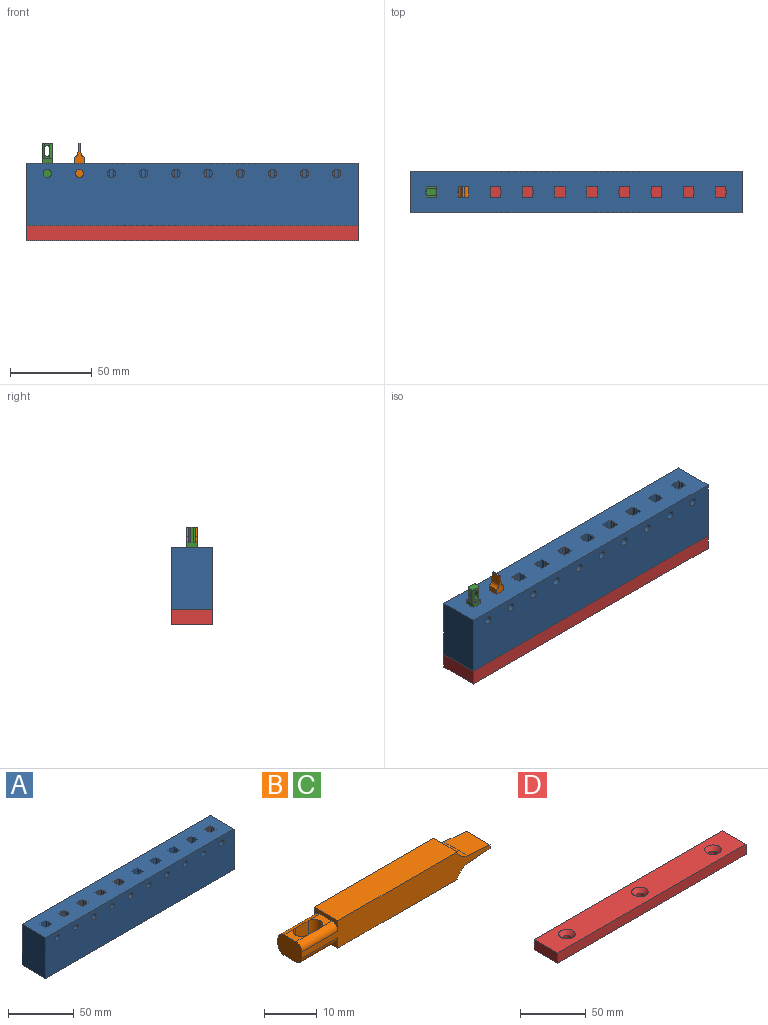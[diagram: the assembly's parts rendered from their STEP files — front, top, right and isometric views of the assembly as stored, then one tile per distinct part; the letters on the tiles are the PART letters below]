
ASSEMBLY  parts=4 mates=9
PART A: 152 faces, bbox 203.2x25.4x38.1 mm
  f0: plane 38.1x2.04mm, normal (0,-1,0), area 77.6mm2, adj f40,f41,f49,f151
  f1: plane 38.1x2.04mm, normal (1,0,0), area 77.6mm2, adj f40,f41,f48,f150
  f2: plane 38.1x2.04mm, normal (0,1,0), area 73mm2, adj f3,f40,f41,f95,f102,f103
  f3: plane 38.1x2.04mm, normal (-1,0,0), area 77.6mm2, adj f2,f40,f41,f149
  f4: plane 38.1x2.04mm, normal (0,-1,0), area 77.6mm2, adj f40,f41,f53,f148
  f5: plane 38.1x2.04mm, normal (1,0,0), area 77.6mm2, adj f40,f41,f52,f147
  f6: plane 38.1x2.04mm, normal (0,1,0), area 73mm2, adj f7,f40,f41,f94,f104,f105
  f7: plane 38.1x2.04mm, normal (-1,0,0), area 77.6mm2, adj f6,f40,f41,f146
  f8: plane 38.1x2.04mm, normal (0,-1,0), area 77.6mm2, adj f40,f41,f57,f145
  f9: plane 38.1x2.04mm, normal (1,0,0), area 77.6mm2, adj f40,f41,f56,f144
  f10: plane 38.1x2.04mm, normal (0,1,0), area 73mm2, adj f11,f40,f41,f93,f106,f107
  f11: plane 38.1x2.04mm, normal (-1,0,0), area 77.6mm2, adj f10,f40,f41,f143
  f12: plane 38.1x2.04mm, normal (0,-1,0), area 77.6mm2, adj f40,f41,f61,f142
  f13: plane 38.1x2.04mm, normal (1,0,0), area 77.6mm2, adj f40,f41,f60,f141
  f14: plane 38.1x2.04mm, normal (0,1,0), area 73mm2, adj f15,f40,f41,f92,f108,f109
  f15: plane 38.1x2.04mm, normal (-1,0,0), area 77.6mm2, adj f14,f40,f41,f140
  f16: plane 38.1x2.04mm, normal (0,-1,0), area 77.6mm2, adj f40,f41,f65,f139
  f17: plane 38.1x2.04mm, normal (1,0,0), area 77.6mm2, adj f40,f41,f64,f138
  f18: plane 38.1x2.04mm, normal (0,1,0), area 73mm2, adj f19,f40,f41,f91,f110,f111
  f19: plane 38.1x2.04mm, normal (-1,0,0), area 77.6mm2, adj f18,f40,f41,f137
  f20: plane 38.1x2.04mm, normal (0,-1,0), area 77.6mm2, adj f40,f41,f69,f136
  f21: plane 38.1x2.04mm, normal (1,0,0), area 77.6mm2, adj f40,f41,f68,f135
  f22: plane 38.1x2.04mm, normal (0,1,0), area 73mm2, adj f23,f40,f41,f90,f112,f113
  f23: plane 38.1x2.04mm, normal (-1,0,0), area 77.6mm2, adj f22,f40,f41,f134
  f24: plane 38.1x2.04mm, normal (0,-1,0), area 77.6mm2, adj f40,f41,f73,f133
  f25: plane 38.1x2.04mm, normal (1,0,0), area 77.6mm2, adj f40,f41,f72,f132
  f26: plane 38.1x2.04mm, normal (0,1,0), area 73mm2, adj f27,f40,f41,f89,f114,f115
  f27: plane 38.1x2.04mm, normal (-1,0,0), area 77.6mm2, adj f26,f40,f41,f131
  f28: plane 38.1x2.04mm, normal (0,-1,0), area 77.6mm2, adj f40,f41,f77,f130
  f29: plane 38.1x2.04mm, normal (1,0,0), area 77.6mm2, adj f40,f41,f76,f129
  f30: plane 38.1x2.04mm, normal (0,1,0), area 73mm2, adj f31,f40,f41,f88,f116,f117
  f31: plane 38.1x2.04mm, normal (-1,0,0), area 77.6mm2, adj f30,f40,f41,f128
  f32: plane 38.1x2.04mm, normal (0,-1,0), area 77.6mm2, adj f40,f41,f81,f127
  f33: plane 38.1x2.04mm, normal (1,0,0), area 77.6mm2, adj f40,f41,f80,f126
  f34: plane 38.1x2.04mm, normal (0,1,0), area 73mm2, adj f35,f40,f41,f87,f118,f119
  f35: plane 38.1x2.04mm, normal (-1,0,0), area 77.6mm2, adj f34,f40,f41,f125
  f36: plane 38.1x2.04mm, normal (0,-1,0), area 77.6mm2, adj f40,f41,f85,f124
  f37: plane 38.1x2.04mm, normal (1,0,0), area 77.6mm2, adj f40,f41,f84,f123
  f38: plane 38.1x2.04mm, normal (0,1,0), area 73mm2, adj f39,f40,f41,f86,f120,f121
  f39: plane 38.1x2.04mm, normal (-1,0,0), area 77.6mm2, adj f38,f40,f41,f122
  f40: plane 203.2x25.4mm, normal (0,0,1), area 4745.9mm2, adj f0,f1,f2,f3,f4,f5,f6,f7
  f41: plane 203.2x25.4mm, normal (0,0,-1), area 4684.5mm2, adj f0,f1,f2,f3,f4,f5,f6,f7
  f42: plane 203.2x38.1mm, normal (0,1,0), area 7741.9mm2, adj f40,f41,f43,f45
  f43: plane 38.1x25.4mm, normal (-1,0,0), area 967.7mm2, adj f40,f41,f42,f44
  f44: plane 203.2x38.1mm, normal (0,-1,0), area 7537.2mm2, adj f40,f41,f43,f45,f86,f87,f88,f89
  f45: plane 38.1x25.4mm, normal (1,0,0), area 967.7mm2, adj f40,f41,f42,f44
  f46: plane 38.1x2.04mm, normal (0,-1,0), area 77.6mm2, adj f40,f41,f47,f151
  f47: plane 38.1x2.04mm, normal (1,0,0), area 77.6mm2, adj f40,f41,f46,f150
  f48: plane 38.1x2.04mm, normal (0,1,0), area 73mm2, adj f1,f40,f41,f95,f102,f103
  f49: plane 38.1x2.04mm, normal (-1,0,0), area 77.6mm2, adj f0,f40,f41,f149
  f50: plane 38.1x2.04mm, normal (0,-1,0), area 77.6mm2, adj f40,f41,f51,f148
  f51: plane 38.1x2.04mm, normal (1,0,0), area 77.6mm2, adj f40,f41,f50,f147
  f52: plane 38.1x2.04mm, normal (0,1,0), area 73mm2, adj f5,f40,f41,f94,f104,f105
  f53: plane 38.1x2.04mm, normal (-1,0,0), area 77.6mm2, adj f4,f40,f41,f146
  f54: plane 38.1x2.04mm, normal (0,-1,0), area 77.6mm2, adj f40,f41,f55,f145
  f55: plane 38.1x2.04mm, normal (1,0,0), area 77.6mm2, adj f40,f41,f54,f144
  f56: plane 38.1x2.04mm, normal (0,1,0), area 73mm2, adj f9,f40,f41,f93,f106,f107
  f57: plane 38.1x2.04mm, normal (-1,0,0), area 77.6mm2, adj f8,f40,f41,f143
  f58: plane 38.1x2.04mm, normal (0,-1,0), area 77.6mm2, adj f40,f41,f59,f142
  f59: plane 38.1x2.04mm, normal (1,0,0), area 77.6mm2, adj f40,f41,f58,f141
  f60: plane 38.1x2.04mm, normal (0,1,0), area 73mm2, adj f13,f40,f41,f92,f108,f109
  f61: plane 38.1x2.04mm, normal (-1,0,0), area 77.6mm2, adj f12,f40,f41,f140
  f62: plane 38.1x2.04mm, normal (0,-1,0), area 77.6mm2, adj f40,f41,f63,f139
  f63: plane 38.1x2.04mm, normal (1,0,0), area 77.6mm2, adj f40,f41,f62,f138
  f64: plane 38.1x2.04mm, normal (0,1,0), area 73mm2, adj f17,f40,f41,f91,f110,f111
  f65: plane 38.1x2.04mm, normal (-1,0,0), area 77.6mm2, adj f16,f40,f41,f137
  f66: plane 38.1x2.04mm, normal (0,-1,0), area 77.6mm2, adj f40,f41,f67,f136
  f67: plane 38.1x2.04mm, normal (1,0,0), area 77.6mm2, adj f40,f41,f66,f135
  f68: plane 38.1x2.04mm, normal (0,1,0), area 73mm2, adj f21,f40,f41,f90,f112,f113
  f69: plane 38.1x2.04mm, normal (-1,0,0), area 77.6mm2, adj f20,f40,f41,f134
  f70: plane 38.1x2.04mm, normal (0,-1,0), area 77.6mm2, adj f40,f41,f71,f133
  f71: plane 38.1x2.04mm, normal (1,0,0), area 77.6mm2, adj f40,f41,f70,f132
  f72: plane 38.1x2.04mm, normal (0,1,0), area 73mm2, adj f25,f40,f41,f89,f114,f115
  f73: plane 38.1x2.04mm, normal (-1,0,0), area 77.6mm2, adj f24,f40,f41,f131
  f74: plane 38.1x2.04mm, normal (0,-1,0), area 77.6mm2, adj f40,f41,f75,f130
  f75: plane 38.1x2.04mm, normal (1,0,0), area 77.6mm2, adj f40,f41,f74,f129
  f76: plane 38.1x2.04mm, normal (0,1,0), area 73mm2, adj f29,f40,f41,f88,f116,f117
  f77: plane 38.1x2.04mm, normal (-1,0,0), area 77.6mm2, adj f28,f40,f41,f128
  f78: plane 38.1x2.04mm, normal (0,-1,0), area 77.6mm2, adj f40,f41,f79,f127
  f79: plane 38.1x2.04mm, normal (1,0,0), area 77.6mm2, adj f40,f41,f78,f126
  f80: plane 38.1x2.04mm, normal (0,1,0), area 73mm2, adj f33,f40,f41,f87,f118,f119
  f81: plane 38.1x2.04mm, normal (-1,0,0), area 77.6mm2, adj f32,f40,f41,f125
  f82: plane 38.1x2.04mm, normal (0,-1,0), area 77.6mm2, adj f40,f41,f83,f124
  f83: plane 38.1x2.04mm, normal (1,0,0), area 77.6mm2, adj f40,f41,f82,f123
  f84: plane 38.1x2.04mm, normal (0,1,0), area 73mm2, adj f37,f40,f41,f86,f120,f121
  f85: plane 38.1x2.04mm, normal (-1,0,0), area 77.6mm2, adj f36,f40,f41,f122
  f86: cylinder r=2.55mm len=9.53mm, axis (0,-1,0), area 152.2mm2, adj f38,f44,f84,f120,f121
  f87: cylinder r=2.55mm len=9.53mm, axis (0,-1,0), area 152.2mm2, adj f34,f44,f80,f118,f119
  f88: cylinder r=2.55mm len=9.53mm, axis (0,-1,0), area 152.2mm2, adj f30,f44,f76,f116,f117
  f89: cylinder r=2.55mm len=9.53mm, axis (0,-1,0), area 152.2mm2, adj f26,f44,f72,f114,f115
  f90: cylinder r=2.55mm len=9.53mm, axis (0,-1,0), area 152.2mm2, adj f22,f44,f68,f112,f113
  f91: cylinder r=2.55mm len=9.53mm, axis (0,-1,0), area 152.2mm2, adj f18,f44,f64,f110,f111
  f92: cylinder r=2.55mm len=9.53mm, axis (0,-1,0), area 152.2mm2, adj f14,f44,f60,f108,f109
  f93: cylinder r=2.55mm len=9.53mm, axis (0,-1,0), area 152.2mm2, adj f10,f44,f56,f106,f107
  f94: cylinder r=2.55mm len=9.53mm, axis (0,-1,0), area 152.2mm2, adj f6,f44,f52,f104,f105
  f95: cylinder r=2.55mm len=9.53mm, axis (0,-1,0), area 152.2mm2, adj f2,f44,f48,f102,f103
  f96: cylinder r=2.55mm len=19.05mm, axis (0,0,-1), area 305.5mm2, adj f41,f97
  f97: plane 5.11x5.11mm, normal (0,0,-1), area 20.5mm2, adj f96
  f98: cylinder r=2.55mm len=19.05mm, axis (0,0,-1), area 305.5mm2, adj f41,f99
  f99: plane 5.11x5.11mm, normal (0,0,-1), area 20.5mm2, adj f98
  f100: cylinder r=2.55mm len=19.05mm, axis (0,0,-1), area 305.5mm2, adj f41,f101
  f101: plane 5.11x5.11mm, normal (0,0,-1), area 20.5mm2, adj f100
  f102: cylinder r=3.37mm len=4.07mm, axis (0,0,1), area 9mm2, adj f2,f40,f48,f95
  f103: cylinder r=3.37mm len=29.47mm, axis (0,0,1), area 68.1mm2, adj f2,f41,f48,f95
  f104: cylinder r=3.37mm len=4.07mm, axis (0,0,1), area 9mm2, adj f6,f40,f52,f94
  f105: cylinder r=3.37mm len=29.47mm, axis (0,0,1), area 68.1mm2, adj f6,f41,f52,f94
  f106: cylinder r=3.37mm len=4.07mm, axis (0,0,1), area 9mm2, adj f10,f40,f56,f93
  f107: cylinder r=3.37mm len=29.47mm, axis (0,0,1), area 68.1mm2, adj f10,f41,f56,f93
  f108: cylinder r=3.37mm len=4.07mm, axis (0,0,1), area 9mm2, adj f14,f40,f60,f92
  f109: cylinder r=3.37mm len=29.47mm, axis (0,0,1), area 68.1mm2, adj f14,f41,f60,f92
  f110: cylinder r=3.37mm len=4.07mm, axis (0,0,1), area 9mm2, adj f18,f40,f64,f91
  f111: cylinder r=3.37mm len=29.47mm, axis (0,0,1), area 68.1mm2, adj f18,f41,f64,f91
  f112: cylinder r=3.37mm len=4.07mm, axis (0,0,1), area 9mm2, adj f22,f40,f68,f90
  f113: cylinder r=3.37mm len=29.47mm, axis (0,0,1), area 68.1mm2, adj f22,f41,f68,f90
  f114: cylinder r=3.37mm len=4.07mm, axis (0,0,1), area 9mm2, adj f26,f40,f72,f89
  f115: cylinder r=3.37mm len=29.47mm, axis (0,0,1), area 68.1mm2, adj f26,f41,f72,f89
  f116: cylinder r=3.37mm len=4.07mm, axis (0,0,1), area 9mm2, adj f30,f40,f76,f88
  f117: cylinder r=3.37mm len=29.47mm, axis (0,0,1), area 68.1mm2, adj f30,f41,f76,f88
  f118: cylinder r=3.37mm len=4.07mm, axis (0,0,1), area 9mm2, adj f34,f40,f80,f87
  f119: cylinder r=3.37mm len=29.47mm, axis (0,0,1), area 68.1mm2, adj f34,f41,f80,f87
  f120: cylinder r=3.37mm len=4.07mm, axis (0,0,1), area 9mm2, adj f38,f40,f84,f86
  f121: cylinder r=3.37mm len=29.47mm, axis (0,0,1), area 68.1mm2, adj f38,f41,f84,f86
  f122: cylinder r=3.37mm len=38.1mm, axis (0,0,1), area 88.5mm2, adj f39,f40,f41,f85
  f123: cylinder r=3.37mm len=38.1mm, axis (0,0,1), area 88.5mm2, adj f37,f40,f41,f83
  f124: cylinder r=3.37mm len=38.1mm, axis (0,0,1), area 88.5mm2, adj f36,f40,f41,f82
  f125: cylinder r=3.37mm len=38.1mm, axis (0,0,1), area 88.5mm2, adj f35,f40,f41,f81
  f126: cylinder r=3.37mm len=38.1mm, axis (0,0,1), area 88.5mm2, adj f33,f40,f41,f79
  f127: cylinder r=3.37mm len=38.1mm, axis (0,0,1), area 88.5mm2, adj f32,f40,f41,f78
  f128: cylinder r=3.37mm len=38.1mm, axis (0,0,1), area 88.5mm2, adj f31,f40,f41,f77
  f129: cylinder r=3.37mm len=38.1mm, axis (0,0,1), area 88.5mm2, adj f29,f40,f41,f75
  f130: cylinder r=3.37mm len=38.1mm, axis (0,0,1), area 88.5mm2, adj f28,f40,f41,f74
  f131: cylinder r=3.37mm len=38.1mm, axis (0,0,1), area 88.5mm2, adj f27,f40,f41,f73
  f132: cylinder r=3.37mm len=38.1mm, axis (0,0,1), area 88.5mm2, adj f25,f40,f41,f71
  f133: cylinder r=3.37mm len=38.1mm, axis (0,0,1), area 88.5mm2, adj f24,f40,f41,f70
  f134: cylinder r=3.37mm len=38.1mm, axis (0,0,1), area 88.5mm2, adj f23,f40,f41,f69
  f135: cylinder r=3.37mm len=38.1mm, axis (0,0,1), area 88.5mm2, adj f21,f40,f41,f67
  f136: cylinder r=3.37mm len=38.1mm, axis (0,0,1), area 88.5mm2, adj f20,f40,f41,f66
  f137: cylinder r=3.37mm len=38.1mm, axis (0,0,1), area 88.5mm2, adj f19,f40,f41,f65
  f138: cylinder r=3.37mm len=38.1mm, axis (0,0,1), area 88.5mm2, adj f17,f40,f41,f63
  f139: cylinder r=3.37mm len=38.1mm, axis (0,0,1), area 88.5mm2, adj f16,f40,f41,f62
  f140: cylinder r=3.37mm len=38.1mm, axis (0,0,1), area 88.5mm2, adj f15,f40,f41,f61
  f141: cylinder r=3.37mm len=38.1mm, axis (0,0,1), area 88.5mm2, adj f13,f40,f41,f59
  f142: cylinder r=3.37mm len=38.1mm, axis (0,0,1), area 88.5mm2, adj f12,f40,f41,f58
  f143: cylinder r=3.37mm len=38.1mm, axis (0,0,1), area 88.5mm2, adj f11,f40,f41,f57
  f144: cylinder r=3.37mm len=38.1mm, axis (0,0,1), area 88.5mm2, adj f9,f40,f41,f55
  f145: cylinder r=3.37mm len=38.1mm, axis (0,0,1), area 88.5mm2, adj f8,f40,f41,f54
  f146: cylinder r=3.37mm len=38.1mm, axis (0,0,1), area 88.5mm2, adj f7,f40,f41,f53
  f147: cylinder r=3.37mm len=38.1mm, axis (0,0,1), area 88.5mm2, adj f5,f40,f41,f51
  f148: cylinder r=3.37mm len=38.1mm, axis (0,0,1), area 88.5mm2, adj f4,f40,f41,f50
  f149: cylinder r=3.37mm len=38.1mm, axis (0,0,1), area 88.5mm2, adj f3,f40,f41,f49
  f150: cylinder r=3.37mm len=38.1mm, axis (0,0,1), area 88.5mm2, adj f1,f40,f41,f47
  f151: cylinder r=3.37mm len=38.1mm, axis (0,0,1), area 88.5mm2, adj f0,f40,f41,f46
PART B: 24 faces, bbox 50.3x6.4x6.4 mm
  f0: plane 50.32x6.35mm, normal (0,1,0), area 233.7mm2, adj f10,f11,f12,f13,f14,f15,f16,f17
  f1: plane 50.32x6.35mm, normal (0,-1,0), area 233.7mm2, adj f10,f11,f12,f13,f14,f15,f16,f17
  f2: plane 3.18x2.83mm, normal (0,0,-1), area 5.9mm2, adj f8,f14,f20,f23
  f3: plane 3.18x2.83mm, normal (0,0,-1), area 5.9mm2, adj f6,f12,f20,f23
  f4: plane 3.18x2.83mm, normal (0,0,1), area 5.9mm2, adj f8,f15,f21,f22
  f5: plane 3.18x2.83mm, normal (0,0,1), area 5.9mm2, adj f6,f12,f21,f22
  f6: cylinder r=1.63mm len=4.67mm, axis (0,0,-1), area 23.8mm2, adj f3,f5,f7,f9,f20,f21,f22,f23
  f7: plane 4.67x3.32mm, normal (0,-1,0), area 15.5mm2, adj f6,f8,f22,f23
  f8: cylinder r=1.63mm len=4.67mm, axis (0,0,-1), area 23.8mm2, adj f2,f4,f7,f9,f20,f21,f22,f23
  f9: plane 4.67x3.3mm, normal (0,1,0), area 15.4mm2, adj f6,f8,f20,f21
  f10: plane 6.35x0.79mm, normal (1,0,0), area 5mm2, adj f0,f1,f16,f18
  f11: plane 31.91x6.35mm, normal (0,0,1), area 202.7mm2, adj f0,f1,f15,f17
  f12: plane 6.35x4.67mm, normal (-1,0,0), area 27.5mm2, adj f0,f1,f3,f5,f20,f21,f22,f23
  f13: plane 31.91x6.35mm, normal (0,0,-1), area 202.7mm2, adj f0,f1,f14,f19
  f14: plane 6.35x2.43mm, normal (-1,0,0), area 6.4mm2, adj f0,f1,f2,f13,f20,f23
  f15: plane 6.35x2.43mm, normal (-1,0,0), area 6.4mm2, adj f0,f1,f4,f11,f21,f22
  f16: plane 6.35x5.99mm, normal (0.09,0,1), area 38.2mm2, adj f0,f1,f10,f17
  f17: cylinder r=3.17mm len=6.35mm, axis (0,-1,0), area 24.1mm2, adj f0,f1,f11,f16
  f18: plane 6.35x5.99mm, normal (0.09,0,-1), area 38.2mm2, adj f0,f1,f10,f19
  f19: cylinder r=3.17mm len=6.35mm, axis (0,-1,0), area 24.1mm2, adj f0,f1,f13,f18
  f20: cylinder r=1.59mm len=9.65mm, axis (-1,0,0), area 23.9mm2, adj f1,f2,f3,f6,f8,f9,f12,f14
  f21: cylinder r=1.59mm len=9.65mm, axis (-1,0,0), area 23.9mm2, adj f1,f4,f5,f6,f8,f9,f12,f15
  f22: cylinder r=1.59mm len=9.65mm, axis (-1,0,0), area 23.9mm2, adj f0,f4,f5,f6,f7,f8,f12,f15
  f23: cylinder r=1.59mm len=9.65mm, axis (-1,0,0), area 23.9mm2, adj f0,f2,f3,f6,f7,f8,f12,f14
PART C: same geometry as B
PART D: 12 faces, bbox 203.2x25.4x9.5 mm
  f0: plane 203.2x9.53mm, normal (0,1,0), area 1935.5mm2, adj f1,f3,f4,f5
  f1: plane 25.4x9.53mm, normal (-1,0,0), area 241.9mm2, adj f0,f2,f4,f5
  f2: plane 203.2x9.53mm, normal (0,-1,0), area 1935.5mm2, adj f1,f3,f4,f5
  f3: plane 25.4x9.53mm, normal (1,0,0), area 241.9mm2, adj f0,f2,f4,f5
  f4: plane 203.2x25.4mm, normal (0,0,1), area 4781.2mm2, adj f0,f1,f2,f3,f7,f9,f11
  f5: plane 203.2x25.4mm, normal (0,0,-1), area 5060.9mm2, adj f0,f1,f2,f3,f6,f8,f10
  f6: cylinder r=3.26mm len=6.53mm, axis (0,0,1), area 122.5mm2, adj f5,f7
  f7: cone r=3.26mm half-angle=41deg, axis (0,0,1), area 142.1mm2, adj f4,f6
  f8: cylinder r=3.26mm len=6.53mm, axis (0,0,1), area 122.5mm2, adj f5,f9
  f9: cone r=3.26mm half-angle=41deg, axis (0,0,1), area 142.1mm2, adj f4,f8
  f10: cylinder r=3.26mm len=6.53mm, axis (0,0,1), area 122.5mm2, adj f5,f11
  f11: cone r=3.26mm half-angle=41deg, axis (0,0,1), area 142.1mm2, adj f4,f10
PLACE A t=(53.16,9.05,28.61)mm
PLACE B rot(axis=(0.71,0,0.71),180deg) t=(-15.74,9.05,40.83)mm
PLACE C rot(axis=(-0.58,0.58,0.58),120deg) t=(-35.42,9.05,66.71)mm
PLACE D rot(axis=(1,0,0),180deg) t=(53.16,9.05,28.61)mm
MATE planar D.f8 <-> A.f41  axis (0,0,1) through (53.16,9.05,28.61)mm
MATE planar B.f0 <-> A.f80  axis (0,-1,0) through (-15.74,5.88,54.29)mm
MATE planar C.f10 <-> D.f8  axis (0,0,-1) through (-35.42,9.05,28.61)mm
MATE planar D.f1 <-> A.f43  axis (-1,0,0) through (-48.44,9.05,23.85)mm
MATE planar C.f11 <-> A.f82  axis (0,1,0) through (-35.42,12.23,53.32)mm
MATE planar B.f13 <-> A.f79  axis (-1,0,0) through (-18.91,9.05,54.22)mm
MATE planar D.f2 <-> A.f42  axis (0,1,0) through (53.16,21.75,23.85)mm
MATE planar B.f12 <-> D.f8  axis (0,0,-1) through (-15.74,9.05,28.61)mm
MATE planar C.f1 <-> A.f85  axis (1,0,0) through (-32.25,9.8,69.28)mm
